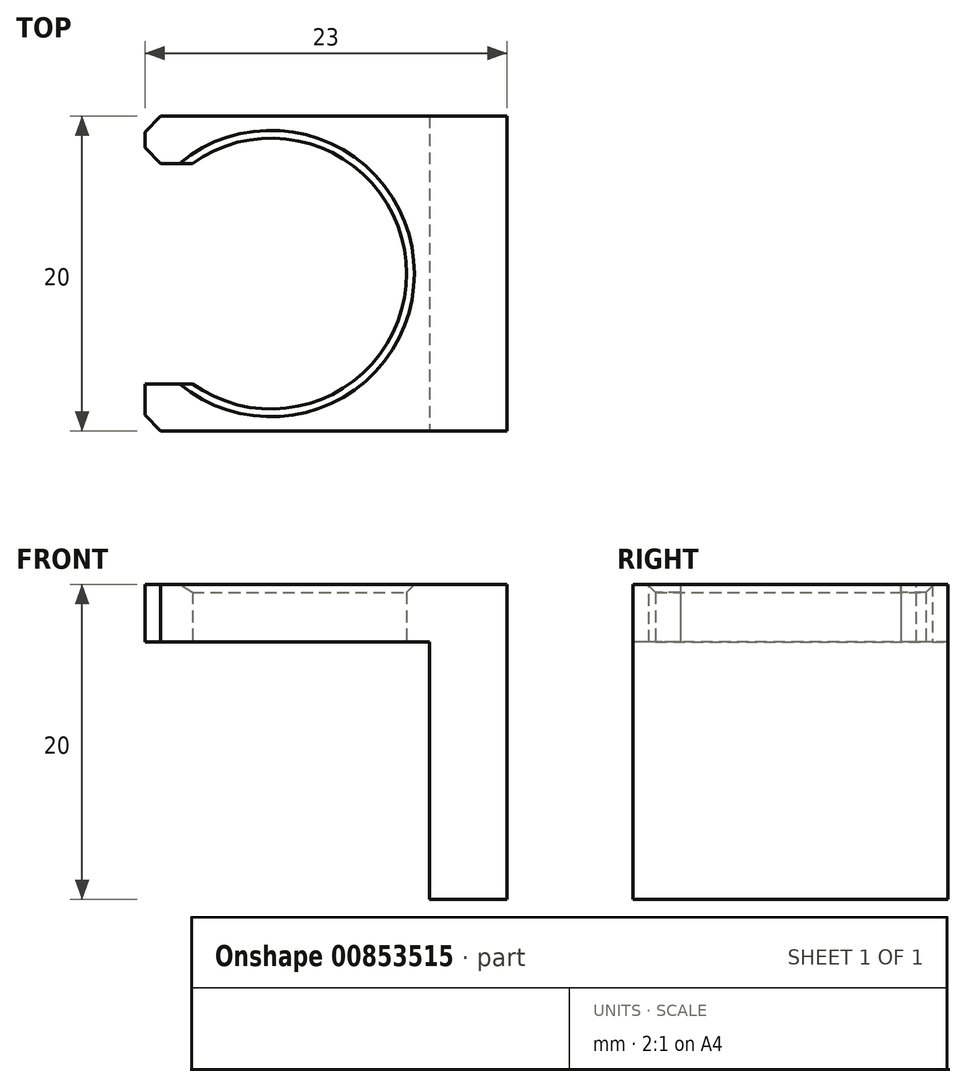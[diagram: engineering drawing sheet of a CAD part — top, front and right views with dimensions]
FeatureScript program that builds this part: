
annotation { "Feature Type Name" : "Feature", "Feature Type Description" : "" }
export const myFeature = defineFeature(function(context is Context, id is Id, definition is map)
    precondition{}
    {
        {
            var Q0;
            Q0=qCreatedBy(makeId("Top.planeOp"),FACE);
            var sketch = newSketch(context, id + "F0", { "sketchPlane" : qUnion([Q0])});
            skArc(sketch, "E0", {"start": v(-5, -7) * mm, "mid": v(8.6, 0) * mm, "end": v(-5, 7) * mm});
            skLineSegment(sketch, "E1.bottom", {"start": v(-8, 10) * mm, "end": v(8, 10) * mm});
            skLineSegment(sketch, "E1.top", {"start": v(-8, -10) * mm, "end": v(8, -10) * mm});
            skLineSegment(sketch, "E1.left", {"start": v(-8, 10) * mm, "end": v(-8, 7) * mm});
            skLineSegment(sketch, "E2.bottom", {"start": v(-8, 7) * mm, "end": v(-5, 7) * mm});
            skLineSegment(sketch, "E2.top", {"start": v(-8, -7) * mm, "end": v(-5, -7) * mm});
            skPoint(sketch, "E2.middle", {"position": v(-6.3, 0) * mm});
            skPoint(sketch, "E2.middle.positionSnap0", {"position": v(-8, 0) * mm});
            skPoint(sketch, "E2.centerSnap0", {"position": v(-8, 0) * mm});
            skLineSegment(sketch, "E3.trimOffspring", {"start": v(-8, -7) * mm, "end": v(-8, -10) * mm});
            skPoint(sketch, "E4.orphan", {"position": v(-4.61, -7) * mm});
            skPoint(sketch, "E5.orphan", {"position": v(-4.61, 7) * mm});
            skLineSegment(sketch, "E6.bottom", {"start": v(8, 10) * mm, "end": v(15, 10) * mm});
            skLineSegment(sketch, "E6.top", {"start": v(8, -10) * mm, "end": v(15, -10) * mm});
            skLineSegment(sketch, "E6.left", {"start": v(8, 10) * mm, "end": v(8, 3.16) * mm, "construction": true});
            skLineSegment(sketch, "E6.right", {"start": v(15, 10) * mm, "end": v(15, -10) * mm});
            skLineSegment(sketch, "E7.trimOffspring", {"start": v(8, -3.16) * mm, "end": v(8, -10) * mm, "construction": true});
            skSolve(sketch);
        }
        {
            var Q0;
            Q0=makeQuery(id+"F0.imprint","IMPRINT",FACE,{"disambiguationData":[TD([[makeQuery(id+"F0.imprint","IMPRINT",EDGE,{"derivedFrom":sQuery(id+"F0.wireOp",EDGE,"E0")}),-1.0]])]});
            extrude(context, id + "F1", {"entities" : qUnion([Q0]), "depth" : 3.65 * mm, "offsetDistance" : 25 * mm});
        }
        {
            var Q0;
            Q0=makeQuery(id+"F1.opExtrude","SWEPT_EDGE",EDGE,{"disambiguationData":[OSD([sQuery(id+"F0.wireOp",EDGE,"E1.bottom"),sQuery(id+"F0.wireOp",EDGE,"E1.left")])]});
            var Q1;
            Q1=makeQuery(id+"F1.opExtrude","SWEPT_EDGE",EDGE,{"disambiguationData":[OSD([sQuery(id+"F0.wireOp",EDGE,"E1.top"),sQuery(id+"F0.wireOp",EDGE,"E1.left")])]});
            chamfer(context, id + "F2", {"entities" : qUnion([Q0, Q1]), "width" : 1 * mm, "tangentPropagation" : true});
        }
        {
            var Q0;
            Q0=makeQuery(id+"F1.opExtrude","CAP_EDGE",EDGE,{"disambiguationData":[OSD([sQuery(id+"F0.wireOp",EDGE,"E0")])],"isStart":false});
            chamfer(context, id + "F3", {"entities" : qUnion([Q0]), "width" : 0.5 * mm, "tangentPropagation" : true});
        }
        {
            var Q0;
            Q0=makeQuery(id+"F1.opExtrude","CAP_FACE",FACE,{"disambiguationData":[OSD([sQuery(id+"F0.wireOp",EDGE,"E0"),sQuery(id+"F0.wireOp",EDGE,"E1.bottom"),sQuery(id+"F0.wireOp",EDGE,"E1.top"),sQuery(id+"F0.wireOp",EDGE,"E1.left"),sQuery(id+"F0.wireOp",EDGE,"E2.bottom"),sQuery(id+"F0.wireOp",EDGE,"E2.top"),sQuery(id+"F0.wireOp",EDGE,"E3.trimOffspring"),sQuery(id+"F0.wireOp",EDGE,"E6.bottom"),sQuery(id+"F0.wireOp",EDGE,"E6.top"),sQuery(id+"F0.wireOp",EDGE,"E6.right")])],"isStart":false});
            var sketch = newSketch(context, id + "F4", { "sketchPlane" : qUnion([Q0])});
            skCircle(sketch, "E8", {"center": v(0, 0) * mm, "radius": 10.07 * mm, "construction": true});
            skLineSegment(sketch, "E9.bottom", {"start": v(15, 10) * mm, "end": v(10.07, 10) * mm});
            skLineSegment(sketch, "E9.top", {"start": v(15, -10) * mm, "end": v(10.08, -10) * mm});
            skLineSegment(sketch, "E9.left", {"start": v(15, 10) * mm, "end": v(15, -10) * mm});
            skLineSegment(sketch, "E9.right", {"start": v(10.07, 10) * mm, "end": v(10.08, -10) * mm});
            skSolve(sketch);
        }
        {
            var Q0;
            Q0=makeQuery(id+"F4.imprint","IMPRINT",FACE,{"disambiguationData":[TD([[makeQuery(id+"F4.imprint","IMPRINT",EDGE,{"derivedFrom":sQuery(id+"F4.wireOp",EDGE,"E9.bottom")}),-1.0]])]});
            extrude(context, id + "F5", {"entities" : qUnion([Q0]), "operationType" : NewBodyOperationType.ADD, "oppositeDirection" : true, "depth" : 20 * mm, "offsetDistance" : 25 * mm});
        }
    });
